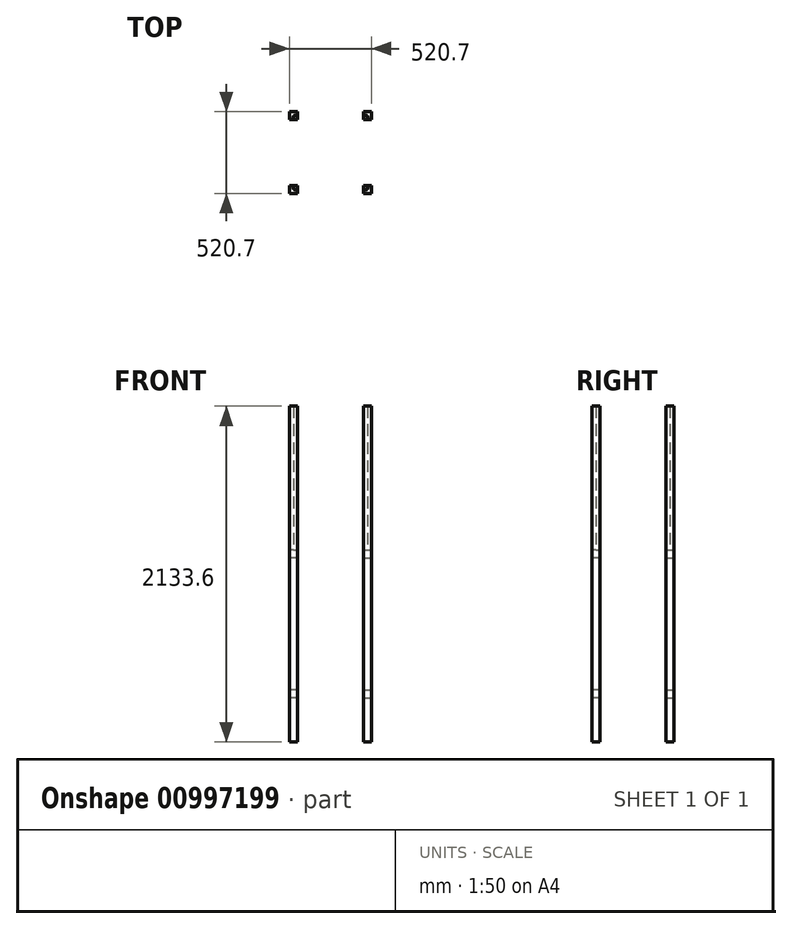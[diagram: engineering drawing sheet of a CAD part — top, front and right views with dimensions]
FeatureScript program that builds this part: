
annotation { "Feature Type Name" : "Feature", "Feature Type Description" : "" }
export const myFeature = defineFeature(function(context is Context, id is Id, definition is map)
    precondition{}
    {
        {
            var Q0;
            Q0=qCreatedBy(makeId("Top.planeOp"),FACE);
            var sketch = newSketch(context, id + "F0", { "sketchPlane" : qUnion([Q0])});
            skLineSegment(sketch, "E0.bottom", {"start": v(0, 0) * mm, "end": v(469.9, 0) * mm});
            skLineSegment(sketch, "E0.top", {"start": v(0, 469.9) * mm, "end": v(469.9, 469.9) * mm});
            skLineSegment(sketch, "E0.left", {"start": v(0, 0) * mm, "end": v(0, 469.9) * mm});
            skLineSegment(sketch, "E0.right", {"start": v(469.9, 0) * mm, "end": v(469.9, 469.9) * mm});
            skLineSegment(sketch, "E1.bottom", {"start": v(25.4, 444.5) * mm, "end": v(-25.4, 444.5) * mm});
            skLineSegment(sketch, "E1.top", {"start": v(25.4, 495.3) * mm, "end": v(-25.4, 495.3) * mm});
            skLineSegment(sketch, "E1.left", {"start": v(25.4, 444.5) * mm, "end": v(25.4, 495.3) * mm});
            skLineSegment(sketch, "E1.right", {"start": v(-25.4, 444.5) * mm, "end": v(-25.4, 495.3) * mm});
            skPoint(sketch, "E1.middle", {"position": v(0, 469.9) * mm});
            skLineSegment(sketch, "E2.bottom", {"start": v(444.5, 444.5) * mm, "end": v(495.3, 444.5) * mm});
            skLineSegment(sketch, "E2.top", {"start": v(444.5, 495.3) * mm, "end": v(495.3, 495.3) * mm});
            skLineSegment(sketch, "E2.left", {"start": v(444.5, 444.5) * mm, "end": v(444.5, 495.3) * mm});
            skLineSegment(sketch, "E2.right", {"start": v(495.3, 444.5) * mm, "end": v(495.3, 495.3) * mm});
            skPoint(sketch, "E2.middle", {"position": v(469.9, 469.9) * mm});
            skLineSegment(sketch, "E3.bottom", {"start": v(25.4, 25.4) * mm, "end": v(-25.4, 25.4) * mm});
            skLineSegment(sketch, "E3.top", {"start": v(25.4, -25.4) * mm, "end": v(-25.4, -25.4) * mm});
            skLineSegment(sketch, "E3.left", {"start": v(25.4, 25.4) * mm, "end": v(25.4, -25.4) * mm});
            skLineSegment(sketch, "E3.right", {"start": v(-25.4, 25.4) * mm, "end": v(-25.4, -25.4) * mm});
            skPoint(sketch, "E3.middle", {"position": v(0, 0) * mm});
            skLineSegment(sketch, "E4.bottom", {"start": v(444.5, 25.4) * mm, "end": v(495.3, 25.4) * mm});
            skLineSegment(sketch, "E4.top", {"start": v(444.5, -25.4) * mm, "end": v(495.3, -25.4) * mm});
            skLineSegment(sketch, "E4.left", {"start": v(444.5, 25.4) * mm, "end": v(444.5, -25.4) * mm});
            skLineSegment(sketch, "E4.right", {"start": v(495.3, 25.4) * mm, "end": v(495.3, -25.4) * mm});
            skPoint(sketch, "E4.middle", {"position": v(469.9, 0) * mm});
            skLineSegment(sketch, "E5", {"start": v(0, 469.9) * mm, "end": v(469.9, 0) * mm, "construction": true});
            skSolve(sketch);
        }
        {
            var Q0;
            {var subQ0=sQuery(id+"F0.wireOp",EDGE,"E3.top");Q0=makeQuery(id+"F0.imprint","IMPRINT",FACE,{"disambiguationData":[TD([[makeQuery(id+"F0.imprint","IMPRINT",EDGE,{"derivedFrom":subQ0}),-1.0]])]});}
            var Q1;
            {var subQ0=sQuery(id+"F0.wireOp",EDGE,"E1.top");Q1=makeQuery(id+"F0.imprint","IMPRINT",FACE,{"disambiguationData":[TD([[makeQuery(id+"F0.imprint","IMPRINT",EDGE,{"derivedFrom":subQ0}),1.0]])]});}
            var Q2;
            {var subQ7=sQuery(id+"F0.wireOp",EDGE,"E2.top");Q2=makeQuery(id+"F0.imprint","IMPRINT",FACE,{"disambiguationData":[TD([[makeQuery(id+"F0.imprint","IMPRINT",EDGE,{"derivedFrom":subQ7}),-1.0]])]});}
            var Q3;
            {var subQ6=sQuery(id+"F0.wireOp",EDGE,"E4.top");Q3=makeQuery(id+"F0.imprint","IMPRINT",FACE,{"disambiguationData":[TD([[makeQuery(id+"F0.imprint","IMPRINT",EDGE,{"derivedFrom":subQ6}),1.0]])]});}
            var Q4;
            {var subQ0=sQuery(id+"F0.wireOp",EDGE,"E0.right");var subQ1=sQuery(id+"F0.wireOp",EDGE,"E0.bottom");var subQ2=makeQuery(id+"F0.imprint","INTERSECT",VERTEX,{"derivedFrom":[subQ1,subQ0]});Q4=makeQuery(id+"F0.imprint","IMPRINT",FACE,{"disambiguationData":[TD([[makeQuery(id+"F0.imprint","IMPRINT",EDGE,{"disambiguationData":[TD([[subQ2,1.0]])],"derivedFrom":subQ1}),1.0]])]});}
            var Q5;
            {var subQ0=sQuery(id+"F0.wireOp",EDGE,"E0.left");var subQ1=sQuery(id+"F0.wireOp",EDGE,"E0.bottom");var subQ2=makeQuery(id+"F0.imprint","INTERSECT",VERTEX,{"derivedFrom":[subQ1,subQ0]});Q5=makeQuery(id+"F0.imprint","IMPRINT",FACE,{"disambiguationData":[TD([[makeQuery(id+"F0.imprint","IMPRINT",EDGE,{"disambiguationData":[TD([[subQ2,-1.0]])],"derivedFrom":subQ1}),1.0]])]});}
            var Q6;
            {var subQ0=sQuery(id+"F0.wireOp",EDGE,"E0.left");var subQ1=sQuery(id+"F0.wireOp",EDGE,"E0.top");var subQ2=makeQuery(id+"F0.imprint","INTERSECT",VERTEX,{"derivedFrom":[subQ1,subQ0]});Q6=makeQuery(id+"F0.imprint","IMPRINT",FACE,{"disambiguationData":[TD([[makeQuery(id+"F0.imprint","IMPRINT",EDGE,{"disambiguationData":[TD([[subQ2,-1.0]])],"derivedFrom":subQ1}),-1.0]])]});}
            var Q7;
            {var subQ0=sQuery(id+"F0.wireOp",EDGE,"E0.right");var subQ1=sQuery(id+"F0.wireOp",EDGE,"E0.top");var subQ2=makeQuery(id+"F0.imprint","INTERSECT",VERTEX,{"derivedFrom":[subQ1,subQ0]});Q7=makeQuery(id+"F0.imprint","IMPRINT",FACE,{"disambiguationData":[TD([[makeQuery(id+"F0.imprint","IMPRINT",EDGE,{"disambiguationData":[TD([[subQ2,1.0]])],"derivedFrom":subQ1}),-1.0]])]});}
            extrude(context, id + "F1", {"entities" : qUnion([Q0, Q1, Q2, Q3, Q4, Q5, Q6, Q7]), "depth" : 2133.6 * mm, "offsetDistance" : 25.4 * mm});
        }
        {
            var Q0;
            {var subQ0=sQuery(id+"F0.wireOp",EDGE,"E3.left");var subQ3=sQuery(id+"F0.wireOp",EDGE,"E0.bottom");var subQ4=makeQuery(id+"F0.imprint","INTERSECT",VERTEX,{"derivedFrom":[subQ3,subQ0]});Q0=makeQuery(id+"F0.imprint","IMPRINT",FACE,{"disambiguationData":[TD([[makeQuery(id+"F0.imprint","IMPRINT",EDGE,{"disambiguationData":[TD([[subQ4,-1.0]])],"derivedFrom":subQ3}),1.0]])]});}
            cPlane(context, id + "F2", {"entities" : qUnion([Q0]), "cplaneType" : CPlaneType.OFFSET, "offset" : 304.8 * mm, "width" : 152.4 * mm, "height" : 152.4 * mm});
        }
        {
            var Q0;
            Q0=qCreatedBy(id+"F2.planeOp",FACE);
            var sketch = newSketch(context, id + "F3", { "sketchPlane" : qUnion([Q0])});
            skLineSegment(sketch, "E6.bottom", {"start": v(0, 0) * mm, "end": v(469.9, 0) * mm});
            skLineSegment(sketch, "E6.top", {"start": v(0, 469.9) * mm, "end": v(469.9, 469.9) * mm});
            skLineSegment(sketch, "E6.left", {"start": v(0, 0) * mm, "end": v(0, 469.9) * mm});
            skLineSegment(sketch, "E6.right", {"start": v(469.9, 0) * mm, "end": v(469.9, 469.9) * mm});
            skLineSegment(sketch, "E7.bottom", {"start": v(25.4, 444.5) * mm, "end": v(-25.4, 444.5) * mm});
            skLineSegment(sketch, "E7.top", {"start": v(25.4, 495.3) * mm, "end": v(-25.4, 495.3) * mm});
            skLineSegment(sketch, "E7.left", {"start": v(25.4, 444.5) * mm, "end": v(25.4, 495.3) * mm});
            skLineSegment(sketch, "E7.right", {"start": v(-25.4, 444.5) * mm, "end": v(-25.4, 495.3) * mm});
            skPoint(sketch, "E7.middle", {"position": v(0, 469.9) * mm});
            skLineSegment(sketch, "E8.bottom", {"start": v(444.5, 444.5) * mm, "end": v(495.3, 444.5) * mm});
            skLineSegment(sketch, "E8.top", {"start": v(444.5, 495.3) * mm, "end": v(495.3, 495.3) * mm});
            skLineSegment(sketch, "E8.left", {"start": v(444.5, 444.5) * mm, "end": v(444.5, 495.3) * mm});
            skLineSegment(sketch, "E8.right", {"start": v(495.3, 444.5) * mm, "end": v(495.3, 495.3) * mm});
            skPoint(sketch, "E8.middle", {"position": v(469.9, 469.9) * mm});
            skLineSegment(sketch, "E9.bottom", {"start": v(25.4, 25.4) * mm, "end": v(-25.4, 25.4) * mm});
            skLineSegment(sketch, "E9.top", {"start": v(25.4, -25.4) * mm, "end": v(-25.4, -25.4) * mm});
            skLineSegment(sketch, "E9.left", {"start": v(25.4, 25.4) * mm, "end": v(25.4, -25.4) * mm});
            skLineSegment(sketch, "E9.right", {"start": v(-25.4, 25.4) * mm, "end": v(-25.4, -25.4) * mm});
            skPoint(sketch, "E9.middle", {"position": v(0, 0) * mm});
            skLineSegment(sketch, "E10.bottom", {"start": v(444.5, 25.4) * mm, "end": v(495.3, 25.4) * mm});
            skLineSegment(sketch, "E10.top", {"start": v(444.5, -25.4) * mm, "end": v(495.3, -25.4) * mm});
            skLineSegment(sketch, "E10.left", {"start": v(444.5, 25.4) * mm, "end": v(444.5, -25.4) * mm});
            skLineSegment(sketch, "E10.right", {"start": v(495.3, 25.4) * mm, "end": v(495.3, -25.4) * mm});
            skPoint(sketch, "E10.middle", {"position": v(469.9, 0) * mm});
            skLineSegment(sketch, "E11", {"start": v(0, 444.5) * mm, "end": v(25.4, 469.9) * mm});
            skLineSegment(sketch, "E12", {"start": v(25.4, 0) * mm, "end": v(0, 25.4) * mm});
            skLineSegment(sketch, "E13", {"start": v(469.9, 444.5) * mm, "end": v(444.5, 469.9) * mm});
            skLineSegment(sketch, "E14", {"start": v(444.5, 0) * mm, "end": v(469.9, 25.4) * mm});
            skLineSegment(sketch, "E15", {"start": v(444.5, -25.4) * mm, "end": v(495.3, 25.4) * mm});
            skLineSegment(sketch, "E16", {"start": v(25.4, -25.4) * mm, "end": v(-25.4, 25.4) * mm});
            skLineSegment(sketch, "E17", {"start": v(-25.4, 444.5) * mm, "end": v(25.4, 495.3) * mm});
            skLineSegment(sketch, "E18", {"start": v(495.3, 444.5) * mm, "end": v(444.5, 495.3) * mm});
            skLineSegment(sketch, "E19", {"start": v(0, 0) * mm, "end": v(469.9, 469.9) * mm});
            skSolve(sketch);
        }
        {
            var Q0;
            {var subQ3=sQuery(id+"F3.wireOp",EDGE,"E13");Q0=makeQuery(id+"F3.imprint","IMPRINT",FACE,{"disambiguationData":[TD([[makeQuery(id+"F3.imprint","IMPRINT",EDGE,{"derivedFrom":subQ3}),1.0]])]});}
            var Q1;
            {var subQ3=sQuery(id+"F3.wireOp",EDGE,"E12");Q1=makeQuery(id+"F3.imprint","IMPRINT",FACE,{"disambiguationData":[TD([[makeQuery(id+"F3.imprint","IMPRINT",EDGE,{"derivedFrom":subQ3}),-1.0]])]});}
            var Q2;
            {var subQ3=sQuery(id+"F3.wireOp",EDGE,"E14");Q2=makeQuery(id+"F3.imprint","IMPRINT",FACE,{"disambiguationData":[TD([[makeQuery(id+"F3.imprint","IMPRINT",EDGE,{"derivedFrom":subQ3}),1.0]])]});}
            var Q3;
            {var subQ0=sQuery(id+"F3.wireOp",EDGE,"E15");var subQ1=sQuery(id+"F3.wireOp",EDGE,"E6.bottom");var subQ2=makeQuery(id+"F3.imprint","INTERSECT",VERTEX,{"derivedFrom":[subQ1,sQuery(id+"F3.wireOp",EDGE,"E6.right"),subQ0]});Q3=makeQuery(id+"F3.imprint","IMPRINT",FACE,{"disambiguationData":[TD([[makeQuery(id+"F3.imprint","IMPRINT",EDGE,{"disambiguationData":[TD([[subQ2,1.0]])],"derivedFrom":subQ1}),-1.0]])]});}
            var Q4;
            {var subQ3=sQuery(id+"F3.wireOp",EDGE,"E14");Q4=makeQuery(id+"F3.imprint","IMPRINT",FACE,{"disambiguationData":[TD([[makeQuery(id+"F3.imprint","IMPRINT",EDGE,{"derivedFrom":subQ3}),-1.0]])]});}
            var Q5;
            {var subQ0=sQuery(id+"F3.wireOp",EDGE,"E15");var subQ1=sQuery(id+"F3.wireOp",EDGE,"E6.right");var subQ2=makeQuery(id+"F3.imprint","INTERSECT",VERTEX,{"derivedFrom":[sQuery(id+"F3.wireOp",EDGE,"E6.bottom"),subQ1,subQ0]});Q5=makeQuery(id+"F3.imprint","IMPRINT",FACE,{"disambiguationData":[TD([[makeQuery(id+"F3.imprint","IMPRINT",EDGE,{"disambiguationData":[TD([[subQ2,-1.0]])],"derivedFrom":subQ1}),-1.0]])]});}
            var Q6;
            {var subQ0=sQuery(id+"F3.wireOp",EDGE,"E16");var subQ1=sQuery(id+"F3.wireOp",EDGE,"E6.bottom");var subQ2=makeQuery(id+"F3.imprint","INTERSECT",VERTEX,{"derivedFrom":[subQ1,sQuery(id+"F3.wireOp",EDGE,"E6.left"),subQ0]});Q6=makeQuery(id+"F3.imprint","IMPRINT",FACE,{"disambiguationData":[TD([[makeQuery(id+"F3.imprint","IMPRINT",EDGE,{"disambiguationData":[TD([[subQ2,-1.0]])],"derivedFrom":subQ1}),-1.0]])]});}
            var Q7;
            {var subQ3=sQuery(id+"F3.wireOp",EDGE,"E12");Q7=makeQuery(id+"F3.imprint","IMPRINT",FACE,{"disambiguationData":[TD([[makeQuery(id+"F3.imprint","IMPRINT",EDGE,{"derivedFrom":subQ3}),1.0]])]});}
            var Q8;
            {var subQ0=sQuery(id+"F3.wireOp",EDGE,"E16");var subQ1=sQuery(id+"F3.wireOp",EDGE,"E6.left");var subQ2=makeQuery(id+"F3.imprint","INTERSECT",VERTEX,{"derivedFrom":[sQuery(id+"F3.wireOp",EDGE,"E6.bottom"),subQ1,subQ0]});Q8=makeQuery(id+"F3.imprint","IMPRINT",FACE,{"disambiguationData":[TD([[makeQuery(id+"F3.imprint","IMPRINT",EDGE,{"disambiguationData":[TD([[subQ2,-1.0]])],"derivedFrom":subQ1}),1.0]])]});}
            var Q9;
            {var subQ3=sQuery(id+"F3.wireOp",EDGE,"E11");Q9=makeQuery(id+"F3.imprint","IMPRINT",FACE,{"disambiguationData":[TD([[makeQuery(id+"F3.imprint","IMPRINT",EDGE,{"derivedFrom":subQ3}),1.0]])]});}
            var Q10;
            {var subQ0=sQuery(id+"F3.wireOp",EDGE,"E17");var subQ1=sQuery(id+"F3.wireOp",EDGE,"E6.top");var subQ2=makeQuery(id+"F3.imprint","INTERSECT",VERTEX,{"derivedFrom":[subQ1,sQuery(id+"F3.wireOp",EDGE,"E6.left"),subQ0]});Q10=makeQuery(id+"F3.imprint","IMPRINT",FACE,{"disambiguationData":[TD([[makeQuery(id+"F3.imprint","IMPRINT",EDGE,{"disambiguationData":[TD([[subQ2,-1.0]])],"derivedFrom":subQ1}),1.0]])]});}
            var Q11;
            {var subQ0=sQuery(id+"F3.wireOp",EDGE,"E17");var subQ1=sQuery(id+"F3.wireOp",EDGE,"E6.left");var subQ2=makeQuery(id+"F3.imprint","INTERSECT",VERTEX,{"derivedFrom":[sQuery(id+"F3.wireOp",EDGE,"E6.top"),subQ1,subQ0]});Q11=makeQuery(id+"F3.imprint","IMPRINT",FACE,{"disambiguationData":[TD([[makeQuery(id+"F3.imprint","IMPRINT",EDGE,{"disambiguationData":[TD([[subQ2,1.0]])],"derivedFrom":subQ1}),1.0]])]});}
            var Q12;
            {var subQ3=sQuery(id+"F3.wireOp",EDGE,"E11");Q12=makeQuery(id+"F3.imprint","IMPRINT",FACE,{"disambiguationData":[TD([[makeQuery(id+"F3.imprint","IMPRINT",EDGE,{"derivedFrom":subQ3}),-1.0]])]});}
            var Q13;
            {var subQ0=sQuery(id+"F3.wireOp",EDGE,"E18");var subQ1=sQuery(id+"F3.wireOp",EDGE,"E6.top");var subQ2=makeQuery(id+"F3.imprint","INTERSECT",VERTEX,{"derivedFrom":[subQ1,sQuery(id+"F3.wireOp",EDGE,"E6.right"),subQ0]});Q13=makeQuery(id+"F3.imprint","IMPRINT",FACE,{"disambiguationData":[TD([[makeQuery(id+"F3.imprint","IMPRINT",EDGE,{"disambiguationData":[TD([[subQ2,1.0]])],"derivedFrom":subQ1}),1.0]])]});}
            var Q14;
            {var subQ0=sQuery(id+"F3.wireOp",EDGE,"E18");var subQ1=sQuery(id+"F3.wireOp",EDGE,"E6.right");var subQ2=makeQuery(id+"F3.imprint","INTERSECT",VERTEX,{"derivedFrom":[sQuery(id+"F3.wireOp",EDGE,"E6.top"),subQ1,subQ0]});Q14=makeQuery(id+"F3.imprint","IMPRINT",FACE,{"disambiguationData":[TD([[makeQuery(id+"F3.imprint","IMPRINT",EDGE,{"disambiguationData":[TD([[subQ2,1.0]])],"derivedFrom":subQ1}),-1.0]])]});}
            var Q15;
            {var subQ3=sQuery(id+"F3.wireOp",EDGE,"E13");Q15=makeQuery(id+"F3.imprint","IMPRINT",FACE,{"disambiguationData":[TD([[makeQuery(id+"F3.imprint","IMPRINT",EDGE,{"derivedFrom":subQ3}),-1.0]])]});}
            extrude(context, id + "F4", {"entities" : qUnion([Q0, Q1, Q2, Q3, Q4, Q5, Q6, Q7, Q8, Q9, Q10, Q11, Q12, Q13, Q14, Q15]), "operationType" : NewBodyOperationType.REMOVE, "oppositeDirection" : true, "depth" : 25.4 * mm, "offsetDistance" : 25.4 * mm, "hasSecondDirection" : true, "secondDirectionOppositeDirection" : false, "secondDirectionDepth" : 25.4 * mm});
        }
        {
            var Q0;
            {var subQ0=sQuery(id+"F0.wireOp",EDGE,"E3.left");var subQ3=sQuery(id+"F0.wireOp",EDGE,"E0.bottom");var subQ4=makeQuery(id+"F0.imprint","INTERSECT",VERTEX,{"derivedFrom":[subQ3,subQ0]});Q0=makeQuery(id+"F0.imprint","IMPRINT",FACE,{"disambiguationData":[TD([[makeQuery(id+"F0.imprint","IMPRINT",EDGE,{"disambiguationData":[TD([[subQ4,-1.0]])],"derivedFrom":subQ3}),1.0]])]});}
            cPlane(context, id + "F5", {"entities" : qUnion([Q0]), "cplaneType" : CPlaneType.OFFSET, "offset" : 1193.8 * mm, "width" : 152.4 * mm, "height" : 152.4 * mm});
        }
        {
            var Q0;
            Q0=qCreatedBy(id+"F5.planeOp",FACE);
            var sketch = newSketch(context, id + "F6", { "sketchPlane" : qUnion([Q0])});
            skLineSegment(sketch, "E20.bottom", {"start": v(0, 0) * mm, "end": v(469.9, 0) * mm});
            skLineSegment(sketch, "E20.top", {"start": v(0, 469.9) * mm, "end": v(469.9, 469.9) * mm});
            skLineSegment(sketch, "E20.left", {"start": v(0, 0) * mm, "end": v(0, 469.9) * mm});
            skLineSegment(sketch, "E20.right", {"start": v(469.9, 0) * mm, "end": v(469.9, 469.9) * mm});
            skLineSegment(sketch, "E21.bottom", {"start": v(25.4, 444.5) * mm, "end": v(-25.4, 444.5) * mm});
            skLineSegment(sketch, "E21.top", {"start": v(25.4, 495.3) * mm, "end": v(-25.4, 495.3) * mm});
            skLineSegment(sketch, "E21.left", {"start": v(25.4, 444.5) * mm, "end": v(25.4, 495.3) * mm});
            skLineSegment(sketch, "E21.right", {"start": v(-25.4, 444.5) * mm, "end": v(-25.4, 495.3) * mm});
            skPoint(sketch, "E21.middle", {"position": v(0, 469.9) * mm});
            skLineSegment(sketch, "E22.bottom", {"start": v(444.5, 444.5) * mm, "end": v(495.3, 444.5) * mm});
            skLineSegment(sketch, "E22.top", {"start": v(444.5, 495.3) * mm, "end": v(495.3, 495.3) * mm});
            skLineSegment(sketch, "E22.left", {"start": v(444.5, 444.5) * mm, "end": v(444.5, 495.3) * mm});
            skLineSegment(sketch, "E22.right", {"start": v(495.3, 444.5) * mm, "end": v(495.3, 495.3) * mm});
            skPoint(sketch, "E22.middle", {"position": v(469.9, 469.9) * mm});
            skLineSegment(sketch, "E23.bottom", {"start": v(25.4, 25.4) * mm, "end": v(-25.4, 25.4) * mm});
            skLineSegment(sketch, "E23.top", {"start": v(25.4, -25.4) * mm, "end": v(-25.4, -25.4) * mm});
            skLineSegment(sketch, "E23.left", {"start": v(25.4, 25.4) * mm, "end": v(25.4, -25.4) * mm});
            skLineSegment(sketch, "E23.right", {"start": v(-25.4, 25.4) * mm, "end": v(-25.4, -25.4) * mm});
            skPoint(sketch, "E23.middle", {"position": v(0, 0) * mm});
            skLineSegment(sketch, "E24.bottom", {"start": v(444.5, 25.4) * mm, "end": v(495.3, 25.4) * mm});
            skLineSegment(sketch, "E24.top", {"start": v(444.5, -25.4) * mm, "end": v(495.3, -25.4) * mm});
            skLineSegment(sketch, "E24.left", {"start": v(444.5, 25.4) * mm, "end": v(444.5, -25.4) * mm});
            skLineSegment(sketch, "E24.right", {"start": v(495.3, 25.4) * mm, "end": v(495.3, -25.4) * mm});
            skPoint(sketch, "E24.middle", {"position": v(469.9, 0) * mm});
            skLineSegment(sketch, "E25", {"start": v(0, 444.5) * mm, "end": v(25.4, 469.9) * mm});
            skLineSegment(sketch, "E26", {"start": v(444.5, 469.9) * mm, "end": v(469.9, 444.5) * mm});
            skLineSegment(sketch, "E27", {"start": v(0, 25.4) * mm, "end": v(25.4, 0) * mm});
            skLineSegment(sketch, "E28", {"start": v(444.5, 0) * mm, "end": v(469.9, 25.4) * mm});
            skLineSegment(sketch, "E29", {"start": v(444.5, -25.4) * mm, "end": v(495.3, 25.4) * mm});
            skLineSegment(sketch, "E30", {"start": v(25.4, -25.4) * mm, "end": v(-25.4, 25.4) * mm});
            skLineSegment(sketch, "E31", {"start": v(-25.4, 444.5) * mm, "end": v(25.4, 495.3) * mm});
            skLineSegment(sketch, "E32", {"start": v(495.3, 444.5) * mm, "end": v(444.5, 495.3) * mm});
            skSolve(sketch);
        }
        {
            var Q0;
            {var subQ3=sQuery(id+"F6.wireOp",EDGE,"E26");Q0=makeQuery(id+"F6.imprint","IMPRINT",FACE,{"disambiguationData":[TD([[makeQuery(id+"F6.imprint","IMPRINT",EDGE,{"derivedFrom":subQ3}),-1.0]])]});}
            var Q1;
            {var subQ3=sQuery(id+"F6.wireOp",EDGE,"E28");Q1=makeQuery(id+"F6.imprint","IMPRINT",FACE,{"disambiguationData":[TD([[makeQuery(id+"F6.imprint","IMPRINT",EDGE,{"derivedFrom":subQ3}),1.0]])]});}
            var Q2;
            {var subQ3=sQuery(id+"F6.wireOp",EDGE,"E27");Q2=makeQuery(id+"F6.imprint","IMPRINT",FACE,{"disambiguationData":[TD([[makeQuery(id+"F6.imprint","IMPRINT",EDGE,{"derivedFrom":subQ3}),1.0]])]});}
            var Q3;
            {var subQ0=sQuery(id+"F6.wireOp",EDGE,"E31");var subQ1=sQuery(id+"F6.wireOp",EDGE,"E20.left");var subQ2=makeQuery(id+"F6.imprint","INTERSECT",VERTEX,{"derivedFrom":[sQuery(id+"F6.wireOp",EDGE,"E20.top"),subQ1,subQ0]});Q3=makeQuery(id+"F6.imprint","IMPRINT",FACE,{"disambiguationData":[TD([[makeQuery(id+"F6.imprint","IMPRINT",EDGE,{"disambiguationData":[TD([[subQ2,1.0]])],"derivedFrom":subQ1}),1.0]])]});}
            var Q4;
            {var subQ0=sQuery(id+"F6.wireOp",EDGE,"E31");var subQ1=sQuery(id+"F6.wireOp",EDGE,"E20.top");var subQ2=makeQuery(id+"F6.imprint","INTERSECT",VERTEX,{"derivedFrom":[subQ1,sQuery(id+"F6.wireOp",EDGE,"E20.left"),subQ0]});Q4=makeQuery(id+"F6.imprint","IMPRINT",FACE,{"disambiguationData":[TD([[makeQuery(id+"F6.imprint","IMPRINT",EDGE,{"disambiguationData":[TD([[subQ2,-1.0]])],"derivedFrom":subQ1}),1.0]])]});}
            var Q5;
            {var subQ3=sQuery(id+"F6.wireOp",EDGE,"E25");Q5=makeQuery(id+"F6.imprint","IMPRINT",FACE,{"disambiguationData":[TD([[makeQuery(id+"F6.imprint","IMPRINT",EDGE,{"derivedFrom":subQ3}),1.0]])]});}
            var Q6;
            {var subQ3=sQuery(id+"F6.wireOp",EDGE,"E25");Q6=makeQuery(id+"F6.imprint","IMPRINT",FACE,{"disambiguationData":[TD([[makeQuery(id+"F6.imprint","IMPRINT",EDGE,{"derivedFrom":subQ3}),-1.0]])]});}
            var Q7;
            {var subQ0=sQuery(id+"F6.wireOp",EDGE,"E32");var subQ1=sQuery(id+"F6.wireOp",EDGE,"E20.top");var subQ2=makeQuery(id+"F6.imprint","INTERSECT",VERTEX,{"derivedFrom":[subQ1,sQuery(id+"F6.wireOp",EDGE,"E20.right"),subQ0]});Q7=makeQuery(id+"F6.imprint","IMPRINT",FACE,{"disambiguationData":[TD([[makeQuery(id+"F6.imprint","IMPRINT",EDGE,{"disambiguationData":[TD([[subQ2,1.0]])],"derivedFrom":subQ1}),1.0]])]});}
            var Q8;
            {var subQ3=sQuery(id+"F6.wireOp",EDGE,"E26");Q8=makeQuery(id+"F6.imprint","IMPRINT",FACE,{"disambiguationData":[TD([[makeQuery(id+"F6.imprint","IMPRINT",EDGE,{"derivedFrom":subQ3}),1.0]])]});}
            var Q9;
            {var subQ0=sQuery(id+"F6.wireOp",EDGE,"E32");var subQ1=sQuery(id+"F6.wireOp",EDGE,"E20.right");var subQ2=makeQuery(id+"F6.imprint","INTERSECT",VERTEX,{"derivedFrom":[sQuery(id+"F6.wireOp",EDGE,"E20.top"),subQ1,subQ0]});Q9=makeQuery(id+"F6.imprint","IMPRINT",FACE,{"disambiguationData":[TD([[makeQuery(id+"F6.imprint","IMPRINT",EDGE,{"disambiguationData":[TD([[subQ2,1.0]])],"derivedFrom":subQ1}),-1.0]])]});}
            var Q10;
            {var subQ0=sQuery(id+"F6.wireOp",EDGE,"E29");var subQ1=sQuery(id+"F6.wireOp",EDGE,"E20.right");var subQ2=makeQuery(id+"F6.imprint","INTERSECT",VERTEX,{"derivedFrom":[sQuery(id+"F6.wireOp",EDGE,"E20.bottom"),subQ1,subQ0]});Q10=makeQuery(id+"F6.imprint","IMPRINT",FACE,{"disambiguationData":[TD([[makeQuery(id+"F6.imprint","IMPRINT",EDGE,{"disambiguationData":[TD([[subQ2,-1.0]])],"derivedFrom":subQ1}),-1.0]])]});}
            var Q11;
            {var subQ3=sQuery(id+"F6.wireOp",EDGE,"E28");Q11=makeQuery(id+"F6.imprint","IMPRINT",FACE,{"disambiguationData":[TD([[makeQuery(id+"F6.imprint","IMPRINT",EDGE,{"derivedFrom":subQ3}),-1.0]])]});}
            var Q12;
            {var subQ0=sQuery(id+"F6.wireOp",EDGE,"E29");var subQ1=sQuery(id+"F6.wireOp",EDGE,"E20.bottom");var subQ2=makeQuery(id+"F6.imprint","INTERSECT",VERTEX,{"derivedFrom":[subQ1,sQuery(id+"F6.wireOp",EDGE,"E20.right"),subQ0]});Q12=makeQuery(id+"F6.imprint","IMPRINT",FACE,{"disambiguationData":[TD([[makeQuery(id+"F6.imprint","IMPRINT",EDGE,{"disambiguationData":[TD([[subQ2,1.0]])],"derivedFrom":subQ1}),-1.0]])]});}
            var Q13;
            {var subQ0=sQuery(id+"F6.wireOp",EDGE,"E30");var subQ1=sQuery(id+"F6.wireOp",EDGE,"E20.bottom");var subQ2=makeQuery(id+"F6.imprint","INTERSECT",VERTEX,{"derivedFrom":[subQ1,sQuery(id+"F6.wireOp",EDGE,"E20.left"),subQ0]});Q13=makeQuery(id+"F6.imprint","IMPRINT",FACE,{"disambiguationData":[TD([[makeQuery(id+"F6.imprint","IMPRINT",EDGE,{"disambiguationData":[TD([[subQ2,-1.0]])],"derivedFrom":subQ1}),-1.0]])]});}
            var Q14;
            {var subQ3=sQuery(id+"F6.wireOp",EDGE,"E27");Q14=makeQuery(id+"F6.imprint","IMPRINT",FACE,{"disambiguationData":[TD([[makeQuery(id+"F6.imprint","IMPRINT",EDGE,{"derivedFrom":subQ3}),-1.0]])]});}
            var Q15;
            {var subQ0=sQuery(id+"F6.wireOp",EDGE,"E30");var subQ1=sQuery(id+"F6.wireOp",EDGE,"E20.left");var subQ2=makeQuery(id+"F6.imprint","INTERSECT",VERTEX,{"derivedFrom":[sQuery(id+"F6.wireOp",EDGE,"E20.bottom"),subQ1,subQ0]});Q15=makeQuery(id+"F6.imprint","IMPRINT",FACE,{"disambiguationData":[TD([[makeQuery(id+"F6.imprint","IMPRINT",EDGE,{"disambiguationData":[TD([[subQ2,-1.0]])],"derivedFrom":subQ1}),1.0]])]});}
            extrude(context, id + "F7", {"entities" : qUnion([Q0, Q1, Q2, Q3, Q4, Q5, Q6, Q7, Q8, Q9, Q10, Q11, Q12, Q13, Q14, Q15]), "operationType" : NewBodyOperationType.REMOVE, "depth" : 25.4 * mm, "offsetDistance" : 25.4 * mm, "hasSecondDirection" : true, "secondDirectionOppositeDirection" : true, "secondDirectionDepth" : 25.4 * mm});
        }
        {
            var Q0;
            {var subQ0=sQuery(id+"F0.wireOp",EDGE,"E3.left");var subQ3=sQuery(id+"F0.wireOp",EDGE,"E0.bottom");var subQ4=makeQuery(id+"F0.imprint","INTERSECT",VERTEX,{"derivedFrom":[subQ3,subQ0]});Q0=makeQuery(id+"F0.imprint","IMPRINT",FACE,{"disambiguationData":[TD([[makeQuery(id+"F0.imprint","IMPRINT",EDGE,{"disambiguationData":[TD([[subQ4,-1.0]])],"derivedFrom":subQ3}),1.0]])]});}
            cPlane(context, id + "F8", {"entities" : qUnion([Q0]), "cplaneType" : CPlaneType.OFFSET, "offset" : 1219.2 * mm, "width" : 152.4 * mm, "height" : 152.4 * mm});
        }
        {
            var Q0;
            Q0=qCreatedBy(id+"F8.planeOp",FACE);
            var sketch = newSketch(context, id + "F9", { "sketchPlane" : qUnion([Q0])});
            skLineSegment(sketch, "E33.bottom", {"start": v(0, 0) * mm, "end": v(469.9, 0) * mm});
            skLineSegment(sketch, "E33.top", {"start": v(0, 469.9) * mm, "end": v(469.9, 469.9) * mm});
            skLineSegment(sketch, "E33.left", {"start": v(0, 0) * mm, "end": v(0, 469.9) * mm});
            skLineSegment(sketch, "E33.right", {"start": v(469.9, 0) * mm, "end": v(469.9, 469.9) * mm});
            skLineSegment(sketch, "E34.bottom", {"start": v(25.4, 444.5) * mm, "end": v(-25.4, 444.5) * mm});
            skLineSegment(sketch, "E34.top", {"start": v(25.4, 495.3) * mm, "end": v(-25.4, 495.3) * mm});
            skLineSegment(sketch, "E34.left", {"start": v(25.4, 444.5) * mm, "end": v(25.4, 495.3) * mm});
            skLineSegment(sketch, "E34.right", {"start": v(-25.4, 444.5) * mm, "end": v(-25.4, 495.3) * mm});
            skPoint(sketch, "E34.middle", {"position": v(0, 469.9) * mm});
            skLineSegment(sketch, "E35.bottom", {"start": v(444.5, 444.5) * mm, "end": v(495.3, 444.5) * mm});
            skLineSegment(sketch, "E35.top", {"start": v(444.5, 495.3) * mm, "end": v(495.3, 495.3) * mm});
            skLineSegment(sketch, "E35.left", {"start": v(444.5, 444.5) * mm, "end": v(444.5, 495.3) * mm});
            skLineSegment(sketch, "E35.right", {"start": v(495.3, 444.5) * mm, "end": v(495.3, 495.3) * mm});
            skPoint(sketch, "E35.middle", {"position": v(469.9, 469.9) * mm});
            skLineSegment(sketch, "E36.bottom", {"start": v(25.4, 25.4) * mm, "end": v(-25.4, 25.4) * mm});
            skLineSegment(sketch, "E36.top", {"start": v(25.4, -25.4) * mm, "end": v(-25.4, -25.4) * mm});
            skLineSegment(sketch, "E36.left", {"start": v(25.4, 25.4) * mm, "end": v(25.4, -25.4) * mm});
            skLineSegment(sketch, "E36.right", {"start": v(-25.4, 25.4) * mm, "end": v(-25.4, -25.4) * mm});
            skPoint(sketch, "E36.middle", {"position": v(0, 0) * mm});
            skLineSegment(sketch, "E37.bottom", {"start": v(444.5, 25.4) * mm, "end": v(495.3, 25.4) * mm});
            skLineSegment(sketch, "E37.top", {"start": v(444.5, -25.4) * mm, "end": v(495.3, -25.4) * mm});
            skLineSegment(sketch, "E37.left", {"start": v(444.5, 25.4) * mm, "end": v(444.5, -25.4) * mm});
            skLineSegment(sketch, "E37.right", {"start": v(495.3, 25.4) * mm, "end": v(495.3, -25.4) * mm});
            skPoint(sketch, "E37.middle", {"position": v(469.9, 0) * mm});
            skSolve(sketch);
        }
        {
            var Q0;
            {var subQ0=sQuery(id+"F9.wireOp",EDGE,"E33.left");var subQ1=sQuery(id+"F9.wireOp",EDGE,"E33.bottom");var subQ2=makeQuery(id+"F9.imprint","INTERSECT",VERTEX,{"derivedFrom":[subQ1,subQ0]});Q0=makeQuery(id+"F9.imprint","IMPRINT",FACE,{"disambiguationData":[TD([[makeQuery(id+"F9.imprint","IMPRINT",EDGE,{"disambiguationData":[TD([[subQ2,-1.0]])],"derivedFrom":subQ1}),1.0]])]});}
            var Q1;
            {var subQ0=sQuery(id+"F9.wireOp",EDGE,"E33.left");var subQ1=sQuery(id+"F9.wireOp",EDGE,"E33.top");var subQ2=makeQuery(id+"F9.imprint","INTERSECT",VERTEX,{"derivedFrom":[subQ1,subQ0]});Q1=makeQuery(id+"F9.imprint","IMPRINT",FACE,{"disambiguationData":[TD([[makeQuery(id+"F9.imprint","IMPRINT",EDGE,{"disambiguationData":[TD([[subQ2,-1.0]])],"derivedFrom":subQ1}),-1.0]])]});}
            var Q2;
            {var subQ0=sQuery(id+"F9.wireOp",EDGE,"E33.right");var subQ1=sQuery(id+"F9.wireOp",EDGE,"E33.top");var subQ2=makeQuery(id+"F9.imprint","INTERSECT",VERTEX,{"derivedFrom":[subQ1,subQ0]});Q2=makeQuery(id+"F9.imprint","IMPRINT",FACE,{"disambiguationData":[TD([[makeQuery(id+"F9.imprint","IMPRINT",EDGE,{"disambiguationData":[TD([[subQ2,1.0]])],"derivedFrom":subQ1}),-1.0]])]});}
            var Q3;
            {var subQ0=sQuery(id+"F9.wireOp",EDGE,"E33.right");var subQ1=sQuery(id+"F9.wireOp",EDGE,"E33.bottom");var subQ2=makeQuery(id+"F9.imprint","INTERSECT",VERTEX,{"derivedFrom":[subQ1,subQ0]});Q3=makeQuery(id+"F9.imprint","IMPRINT",FACE,{"disambiguationData":[TD([[makeQuery(id+"F9.imprint","IMPRINT",EDGE,{"disambiguationData":[TD([[subQ2,1.0]])],"derivedFrom":subQ1}),1.0]])]});}
            extrude(context, id + "F10", {"entities" : qUnion([Q0, Q1, Q2, Q3]), "operationType" : NewBodyOperationType.REMOVE, "depth" : 914.4 * mm, "offsetDistance" : 25.4 * mm});
        }
    });
